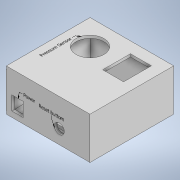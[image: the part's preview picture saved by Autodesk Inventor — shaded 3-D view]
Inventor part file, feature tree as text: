
AUTODESK INVENTOR PART (.ipt)
format: ipt  version: 2020 (Build 240168000, 168)  size: 202,752 bytes
history: native  units: in
note: dims shown in document units (in); Inventor stores cm internally (conversion verified against a paired STEP export)
features: other x4, extrude x4, sketch x4
ambient origin geometry x8: Origin, YZ Plane, XZ Plane, XY Plane, X Axis, Y Axis, Z Axis, Center Point
bodies: Solid1 (feature_tree)
feature tree (12):
  other  "Annotations"
  extrude  "Bottom"  Depth=2.3622in
  extrude  "Walls"  Depth=1.0236in TaperAngle=0.0deg
  extrude  "AC/Reset"  Depth=0.7874in
  extrude  "Extrusion4"  Depth=0.0787in TaperAngle=0.0deg
  sketch  "Sketch1"  dims[d0=2.3622in d1=2.3622in]
  sketch  "Sketch2"  dims[d2=0.0787in d3=0.0in d4=1.0236in d5=0.0in]
  sketch  "Sketch3"  dims[d6=0.3937in d7=0.0in d8=0.7874in]
  sketch  "Sketch4"  dims[d9=2.3622in d10=0.0787in d11=0.0in d12=1.1132in d13=0.2238in d14=0.1266in]
  other  "Leader Text 1"
  other  "Leader Text 2"
  other  "Leader Text 3"
